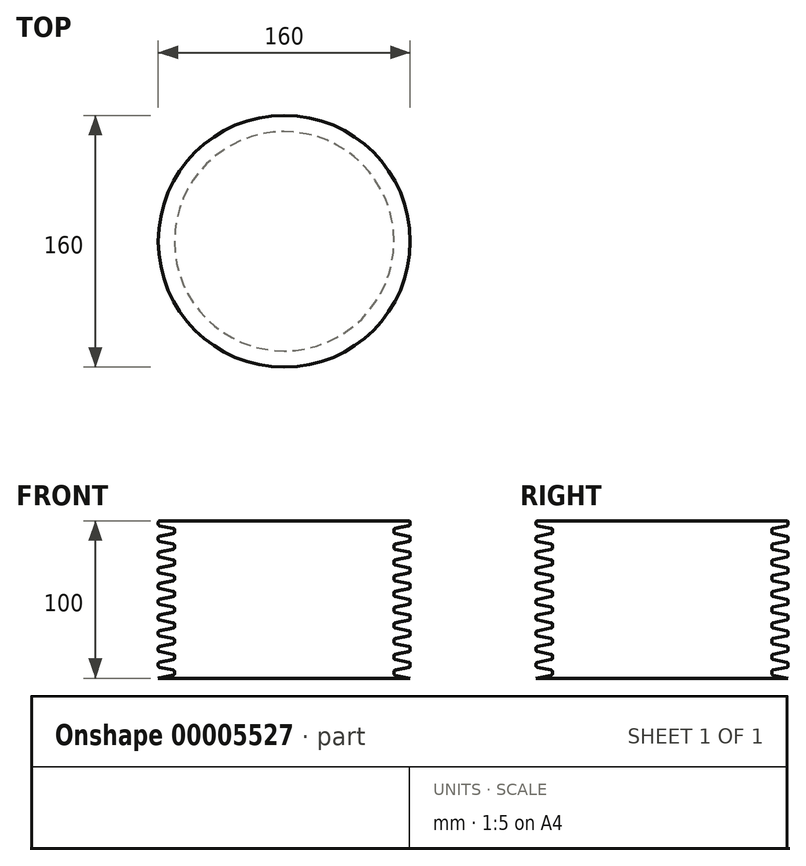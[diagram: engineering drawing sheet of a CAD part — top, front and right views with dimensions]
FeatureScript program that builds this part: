
annotation { "Feature Type Name" : "Feature", "Feature Type Description" : "" }
export const myFeature = defineFeature(function(context is Context, id is Id, definition is map)
    precondition{}
    {
        {
            var Q0;
            Q0=qCreatedBy(makeId("Front.planeOp"),FACE);
            var sketch = newSketch(context, id + "F0", { "sketchPlane" : qUnion([Q0])});
            skLineSegment(sketch, "E0", {"start": v(-80, 0) * mm, "end": v(-69.66, 2.02) * mm});
            skLineSegment(sketch, "E1", {"start": v(-69.66, 2.02) * mm, "end": v(-69.66, 5.02) * mm});
            skLineSegment(sketch, "E2", {"start": v(-69.66, 5.02) * mm, "end": v(-80, 7) * mm});
            skLineSegment(sketch, "E3", {"start": v(-80, 7) * mm, "end": v(-80, 10) * mm});
            skLineSegment(sketch, "E4.0.1.0", {"start": v(-80, 10) * mm, "end": v(-69.66, 12.02) * mm});
            skLineSegment(sketch, "E4.0.1.1", {"start": v(-69.66, 15.02) * mm, "end": v(-80, 17) * mm});
            skLineSegment(sketch, "E4.0.1.2", {"start": v(-80, 17) * mm, "end": v(-80, 20) * mm});
            skLineSegment(sketch, "E4.0.1.3", {"start": v(-69.66, 12.02) * mm, "end": v(-69.66, 15.02) * mm});
            skLineSegment(sketch, "E4.0.2.0", {"start": v(-80, 20) * mm, "end": v(-69.66, 22.02) * mm});
            skLineSegment(sketch, "E4.0.2.1", {"start": v(-69.66, 25.02) * mm, "end": v(-80, 27) * mm});
            skLineSegment(sketch, "E4.0.2.2", {"start": v(-80, 27) * mm, "end": v(-80, 30) * mm});
            skLineSegment(sketch, "E4.0.2.3", {"start": v(-69.66, 22.02) * mm, "end": v(-69.66, 25.02) * mm});
            skLineSegment(sketch, "E4.0.3.0", {"start": v(-80, 30) * mm, "end": v(-69.66, 32.02) * mm});
            skLineSegment(sketch, "E4.0.3.1", {"start": v(-69.66, 35.02) * mm, "end": v(-80, 37) * mm});
            skLineSegment(sketch, "E4.0.3.2", {"start": v(-80, 37) * mm, "end": v(-80, 40) * mm});
            skLineSegment(sketch, "E4.0.3.3", {"start": v(-69.66, 32.02) * mm, "end": v(-69.66, 35.02) * mm});
            skLineSegment(sketch, "E4.0.4.0", {"start": v(-80, 40) * mm, "end": v(-69.66, 42.02) * mm});
            skLineSegment(sketch, "E4.0.4.1", {"start": v(-69.66, 45.02) * mm, "end": v(-80, 47) * mm});
            skLineSegment(sketch, "E4.0.4.2", {"start": v(-80, 47) * mm, "end": v(-80, 50) * mm});
            skLineSegment(sketch, "E4.0.4.3", {"start": v(-69.66, 42.02) * mm, "end": v(-69.66, 45.02) * mm});
            skLineSegment(sketch, "E4.0.5.0", {"start": v(-80, 50) * mm, "end": v(-69.66, 52.02) * mm});
            skLineSegment(sketch, "E4.0.5.1", {"start": v(-69.66, 55.02) * mm, "end": v(-80, 57) * mm});
            skLineSegment(sketch, "E4.0.5.2", {"start": v(-80, 57) * mm, "end": v(-80, 60) * mm});
            skLineSegment(sketch, "E4.0.5.3", {"start": v(-69.66, 52.02) * mm, "end": v(-69.66, 55.02) * mm});
            skLineSegment(sketch, "E4.0.6.0", {"start": v(-80, 60) * mm, "end": v(-69.66, 62.02) * mm});
            skLineSegment(sketch, "E4.0.6.1", {"start": v(-69.66, 65.02) * mm, "end": v(-80, 67) * mm});
            skLineSegment(sketch, "E4.0.6.2", {"start": v(-80, 67) * mm, "end": v(-80, 70) * mm});
            skLineSegment(sketch, "E4.0.6.3", {"start": v(-69.66, 62.02) * mm, "end": v(-69.66, 65.02) * mm});
            skLineSegment(sketch, "E4.direction1", {"start": v(-80, 0) * mm, "end": v(-14, 0) * mm, "construction": true});
            skLineSegment(sketch, "E4.direction2", {"start": v(-80, 0) * mm, "end": v(-80, 10) * mm, "construction": true});
            skLineSegment(sketch, "E5", {"start": v(-80, 0) * mm, "end": v(0, 0) * mm});
            skLineSegment(sketch, "E6.0.0.7", {"start": v(-80, 70) * mm, "end": v(-69.66, 72.02) * mm});
            skLineSegment(sketch, "E6.3.0.7", {"start": v(-69.66, 75.02) * mm, "end": v(-80, 77) * mm});
            skLineSegment(sketch, "E6.6.0.7", {"start": v(-80, 77) * mm, "end": v(-80, 80) * mm});
            skLineSegment(sketch, "E6.9.0.7", {"start": v(-69.66, 72.02) * mm, "end": v(-69.66, 75.02) * mm});
            skLineSegment(sketch, "E6.0.0.8", {"start": v(-80, 80) * mm, "end": v(-69.66, 82.02) * mm});
            skLineSegment(sketch, "E6.3.0.8", {"start": v(-69.66, 85.02) * mm, "end": v(-80, 87) * mm});
            skLineSegment(sketch, "E6.6.0.8", {"start": v(-80, 87) * mm, "end": v(-80, 90) * mm});
            skLineSegment(sketch, "E6.9.0.8", {"start": v(-69.66, 82.02) * mm, "end": v(-69.66, 85.02) * mm});
            skLineSegment(sketch, "E6.0.0.9", {"start": v(-80, 90) * mm, "end": v(-69.66, 92.02) * mm});
            skLineSegment(sketch, "E6.3.0.9", {"start": v(-69.66, 95.02) * mm, "end": v(-80, 97) * mm});
            skLineSegment(sketch, "E6.6.0.9", {"start": v(-80, 97) * mm, "end": v(-80, 100) * mm});
            skLineSegment(sketch, "E6.9.0.9", {"start": v(-69.66, 92.02) * mm, "end": v(-69.66, 95.02) * mm});
            skLineSegment(sketch, "E7", {"start": v(-80, 100) * mm, "end": v(0, 100) * mm});
            skLineSegment(sketch, "E8", {"start": v(0, 100) * mm, "end": v(0, 0) * mm});
            skSolve(sketch);
        }
        {
            var Q0;
            Q0=makeQuery(id+"F0.imprint","IMPRINT",FACE,{"disambiguationData":[TD([[makeQuery(id+"F0.imprint","IMPRINT",EDGE,{"derivedFrom":sQuery(id+"F0.wireOp",EDGE,"E0")}),-1.0]])]});
            var Q1;
            Q1=sQuery(id+"F0.wireOp",EDGE,"E8");
            revolve(context, id + "F1", {"entities" : qUnion([Q0]), "axis" : qUnion([Q1]), "revolveType" : RevolveType.FULL});
        }
        {
            var Q0;
            Q0=makeQuery(id+"F1.opRevolve","SWEPT_EDGE",EDGE,{"disambiguationData":[OSD([sQuery(id+"F0.wireOp",EDGE,"E4.0.6.1"),sQuery(id+"F0.wireOp",EDGE,"E4.0.6.2")])]});
            var Q1;
            {var subQ0=sQuery(id+"F0.wireOp",EDGE,"E4.0.6.2");Q1=qUnion([makeQuery(id+"F1.opRevolve","SWEPT_EDGE",EDGE,{"disambiguationData":[OSD([sQuery(id+"F0.wireOp",EDGE,"E4.0.6.1"),subQ0])]}),makeQuery(id+"F1.opRevolve","SWEPT_EDGE",EDGE,{"disambiguationData":[OSD([subQ0,sQuery(id+"F0.wireOp",EDGE,"E6.0.0.7")])]})]);}
            var Q2;
            Q2=makeQuery(id+"F1.opRevolve","SWEPT_EDGE",EDGE,{"disambiguationData":[OSD([sQuery(id+"F0.wireOp",EDGE,"E4.0.6.1"),sQuery(id+"F0.wireOp",EDGE,"E4.0.6.3")])]});
            var Q3;
            Q3=makeQuery(id+"F1.opRevolve","SWEPT_EDGE",EDGE,{"disambiguationData":[OSD([sQuery(id+"F0.wireOp",EDGE,"E4.0.6.0"),sQuery(id+"F0.wireOp",EDGE,"E4.0.6.3")])]});
            var Q4;
            Q4=makeQuery(id+"F1.opRevolve","SWEPT_EDGE",EDGE,{"disambiguationData":[OSD([sQuery(id+"F0.wireOp",EDGE,"E4.0.5.2"),sQuery(id+"F0.wireOp",EDGE,"E4.0.6.0")])]});
            var Q5;
            Q5=makeQuery(id+"F1.opRevolve","SWEPT_FACE",FACE,{"disambiguationData":[OSD([sQuery(id+"F0.wireOp",EDGE,"E4.0.5.2")])]});
            var Q6;
            Q6=makeQuery(id+"F1.opRevolve","SWEPT_EDGE",EDGE,{"disambiguationData":[OSD([sQuery(id+"F0.wireOp",EDGE,"E4.0.5.1"),sQuery(id+"F0.wireOp",EDGE,"E4.0.5.2")])]});
            var Q7;
            Q7=makeQuery(id+"F1.opRevolve","SWEPT_EDGE",EDGE,{"disambiguationData":[OSD([sQuery(id+"F0.wireOp",EDGE,"E4.0.4.2"),sQuery(id+"F0.wireOp",EDGE,"E4.0.5.0")])]});
            var Q8;
            Q8=makeQuery(id+"F1.opRevolve","SWEPT_EDGE",EDGE,{"disambiguationData":[OSD([sQuery(id+"F0.wireOp",EDGE,"E4.0.4.1"),sQuery(id+"F0.wireOp",EDGE,"E4.0.4.2")])]});
            var Q9;
            Q9=makeQuery(id+"F1.opRevolve","SWEPT_EDGE",EDGE,{"disambiguationData":[OSD([sQuery(id+"F0.wireOp",EDGE,"E4.0.3.2"),sQuery(id+"F0.wireOp",EDGE,"E4.0.4.0")])]});
            var Q10;
            Q10=makeQuery(id+"F1.opRevolve","SWEPT_EDGE",EDGE,{"disambiguationData":[OSD([sQuery(id+"F0.wireOp",EDGE,"E4.0.3.1"),sQuery(id+"F0.wireOp",EDGE,"E4.0.3.2")])]});
            var Q11;
            Q11=makeQuery(id+"F1.opRevolve","SWEPT_EDGE",EDGE,{"disambiguationData":[OSD([sQuery(id+"F0.wireOp",EDGE,"E4.0.3.0"),sQuery(id+"F0.wireOp",EDGE,"E4.0.3.3")])]});
            var Q12;
            Q12=makeQuery(id+"F1.opRevolve","SWEPT_EDGE",EDGE,{"disambiguationData":[OSD([sQuery(id+"F0.wireOp",EDGE,"E4.0.3.1"),sQuery(id+"F0.wireOp",EDGE,"E4.0.3.3")])]});
            var Q13;
            Q13=makeQuery(id+"F1.opRevolve","SWEPT_EDGE",EDGE,{"disambiguationData":[OSD([sQuery(id+"F0.wireOp",EDGE,"E4.0.4.0"),sQuery(id+"F0.wireOp",EDGE,"E4.0.4.3")])]});
            var Q14;
            Q14=makeQuery(id+"F1.opRevolve","SWEPT_EDGE",EDGE,{"disambiguationData":[OSD([sQuery(id+"F0.wireOp",EDGE,"E4.0.4.1"),sQuery(id+"F0.wireOp",EDGE,"E4.0.4.3")])]});
            var Q15;
            Q15=makeQuery(id+"F1.opRevolve","SWEPT_EDGE",EDGE,{"disambiguationData":[OSD([sQuery(id+"F0.wireOp",EDGE,"E4.0.5.0"),sQuery(id+"F0.wireOp",EDGE,"E4.0.5.3")])]});
            var Q16;
            Q16=makeQuery(id+"F1.opRevolve","SWEPT_EDGE",EDGE,{"disambiguationData":[OSD([sQuery(id+"F0.wireOp",EDGE,"E4.0.5.1"),sQuery(id+"F0.wireOp",EDGE,"E4.0.5.3")])]});
            var Q17;
            Q17=makeQuery(id+"F1.opRevolve","SWEPT_EDGE",EDGE,{"disambiguationData":[OSD([sQuery(id+"F0.wireOp",EDGE,"E4.0.2.2"),sQuery(id+"F0.wireOp",EDGE,"E4.0.3.0")])]});
            var Q18;
            Q18=makeQuery(id+"F1.opRevolve","SWEPT_EDGE",EDGE,{"disambiguationData":[OSD([sQuery(id+"F0.wireOp",EDGE,"E4.0.2.1"),sQuery(id+"F0.wireOp",EDGE,"E4.0.2.2")])]});
            var Q19;
            Q19=makeQuery(id+"F1.opRevolve","SWEPT_EDGE",EDGE,{"disambiguationData":[OSD([sQuery(id+"F0.wireOp",EDGE,"E4.0.2.1"),sQuery(id+"F0.wireOp",EDGE,"E4.0.2.3")])]});
            var Q20;
            Q20=makeQuery(id+"F1.opRevolve","SWEPT_EDGE",EDGE,{"disambiguationData":[OSD([sQuery(id+"F0.wireOp",EDGE,"E4.0.2.0"),sQuery(id+"F0.wireOp",EDGE,"E4.0.2.3")])]});
            var Q21;
            Q21=makeQuery(id+"F1.opRevolve","SWEPT_FACE",FACE,{"disambiguationData":[OSD([sQuery(id+"F0.wireOp",EDGE,"E4.0.2.0")])]});
            var Q22;
            Q22=makeQuery(id+"F1.opRevolve","SWEPT_EDGE",EDGE,{"disambiguationData":[OSD([sQuery(id+"F0.wireOp",EDGE,"E4.0.1.2"),sQuery(id+"F0.wireOp",EDGE,"E4.0.2.0")])]});
            var Q23;
            Q23=makeQuery(id+"F1.opRevolve","SWEPT_EDGE",EDGE,{"disambiguationData":[OSD([sQuery(id+"F0.wireOp",EDGE,"E4.0.1.1"),sQuery(id+"F0.wireOp",EDGE,"E4.0.1.2")])]});
            var Q24;
            Q24=makeQuery(id+"F1.opRevolve","SWEPT_EDGE",EDGE,{"disambiguationData":[OSD([sQuery(id+"F0.wireOp",EDGE,"E4.0.1.0"),sQuery(id+"F0.wireOp",EDGE,"E4.0.1.3")])]});
            var Q25;
            Q25=makeQuery(id+"F1.opRevolve","SWEPT_EDGE",EDGE,{"disambiguationData":[OSD([sQuery(id+"F0.wireOp",EDGE,"E4.0.1.1"),sQuery(id+"F0.wireOp",EDGE,"E4.0.1.3")])]});
            var Q26;
            Q26=makeQuery(id+"F1.opRevolve","SWEPT_EDGE",EDGE,{"disambiguationData":[OSD([sQuery(id+"F0.wireOp",EDGE,"E3"),sQuery(id+"F0.wireOp",EDGE,"E4.0.1.0")])]});
            var Q27;
            Q27=makeQuery(id+"F1.opRevolve","SWEPT_EDGE",EDGE,{"disambiguationData":[OSD([sQuery(id+"F0.wireOp",EDGE,"E2"),sQuery(id+"F0.wireOp",EDGE,"E3")])]});
            var Q28;
            Q28=makeQuery(id+"F1.opRevolve","SWEPT_EDGE",EDGE,{"disambiguationData":[OSD([sQuery(id+"F0.wireOp",EDGE,"E1"),sQuery(id+"F0.wireOp",EDGE,"E2")])]});
            var Q29;
            Q29=makeQuery(id+"F1.opRevolve","SWEPT_EDGE",EDGE,{"disambiguationData":[OSD([sQuery(id+"F0.wireOp",EDGE,"E0"),sQuery(id+"F0.wireOp",EDGE,"E1")])]});
            var Q30;
            Q30=makeQuery(id+"F1.opRevolve","SWEPT_EDGE",EDGE,{"disambiguationData":[OSD([sQuery(id+"F0.wireOp",EDGE,"E6.0.0.7"),sQuery(id+"F0.wireOp",EDGE,"E6.9.0.7")])]});
            var Q31;
            Q31=makeQuery(id+"F1.opRevolve","SWEPT_EDGE",EDGE,{"disambiguationData":[OSD([sQuery(id+"F0.wireOp",EDGE,"E6.3.0.7"),sQuery(id+"F0.wireOp",EDGE,"E6.9.0.7")])]});
            var Q32;
            Q32=makeQuery(id+"F1.opRevolve","SWEPT_EDGE",EDGE,{"disambiguationData":[OSD([sQuery(id+"F0.wireOp",EDGE,"E6.3.0.7"),sQuery(id+"F0.wireOp",EDGE,"E6.6.0.7")])]});
            var Q33;
            Q33=makeQuery(id+"F1.opRevolve","SWEPT_EDGE",EDGE,{"disambiguationData":[OSD([sQuery(id+"F0.wireOp",EDGE,"E6.6.0.7"),sQuery(id+"F0.wireOp",EDGE,"E6.0.0.8")])]});
            var Q34;
            Q34=makeQuery(id+"F1.opRevolve","SWEPT_EDGE",EDGE,{"disambiguationData":[OSD([sQuery(id+"F0.wireOp",EDGE,"E6.3.0.8"),sQuery(id+"F0.wireOp",EDGE,"E6.6.0.8")])]});
            var Q35;
            Q35=makeQuery(id+"F1.opRevolve","SWEPT_EDGE",EDGE,{"disambiguationData":[OSD([sQuery(id+"F0.wireOp",EDGE,"E6.6.0.8"),sQuery(id+"F0.wireOp",EDGE,"E6.0.0.9")])]});
            var Q36;
            Q36=makeQuery(id+"F1.opRevolve","SWEPT_EDGE",EDGE,{"disambiguationData":[OSD([sQuery(id+"F0.wireOp",EDGE,"E6.3.0.9"),sQuery(id+"F0.wireOp",EDGE,"E6.6.0.9")])]});
            var Q37;
            Q37=makeQuery(id+"F1.opRevolve","SWEPT_EDGE",EDGE,{"disambiguationData":[OSD([sQuery(id+"F0.wireOp",EDGE,"E6.6.0.9"),sQuery(id+"F0.wireOp",EDGE,"E7")])]});
            var Q38;
            Q38=makeQuery(id+"F1.opRevolve","SWEPT_EDGE",EDGE,{"disambiguationData":[OSD([sQuery(id+"F0.wireOp",EDGE,"E6.3.0.9"),sQuery(id+"F0.wireOp",EDGE,"E6.9.0.9")])]});
            var Q39;
            Q39=makeQuery(id+"F1.opRevolve","SWEPT_EDGE",EDGE,{"disambiguationData":[OSD([sQuery(id+"F0.wireOp",EDGE,"E6.3.0.8"),sQuery(id+"F0.wireOp",EDGE,"E6.9.0.8")])]});
            var Q40;
            Q40=makeQuery(id+"F1.opRevolve","SWEPT_EDGE",EDGE,{"disambiguationData":[OSD([sQuery(id+"F0.wireOp",EDGE,"E6.0.0.9"),sQuery(id+"F0.wireOp",EDGE,"E6.9.0.9")])]});
            var Q41;
            Q41=makeQuery(id+"F1.opRevolve","SWEPT_EDGE",EDGE,{"disambiguationData":[OSD([sQuery(id+"F0.wireOp",EDGE,"E6.0.0.8"),sQuery(id+"F0.wireOp",EDGE,"E6.9.0.8")])]});
            fillet(context, id + "F2", {"entities" : qUnion([Q0, Q1, Q2, Q3, Q4, Q5, Q6, Q7, Q8, Q9, Q10, Q11, Q12, Q13, Q14, Q15, Q16, Q17, Q18, Q19, Q20, Q21, Q22, Q23, Q24, Q25, Q26, Q27, Q28, Q29, Q30, Q31, Q32, Q33, Q34, Q35, Q36, Q37, Q38, Q39, Q40, Q41]), "radius" : 1 * mm, "tangentPropagation" : true, "allowEdgeOverflow" : false});
        }
    });
